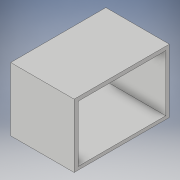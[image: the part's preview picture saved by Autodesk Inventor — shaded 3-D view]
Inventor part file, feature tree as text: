
AUTODESK INVENTOR PART (.ipt)
format: ipt  version: 2019 (Build 230136000, 136)  size: 93,696 bytes
history: native  units: mm
features: extrude x2, sketch x2
ambient origin geometry x8: Origin, YZ Plane, XZ Plane, XY Plane, X Axis, Y Axis, Z Axis, Center Point
bodies: Solid1 (feature_tree)
feature tree (4):
  extrude  "Extrusion1"  Depth=30.0mm
  extrude  "Extrusion2"  Depth=18.0mm TaperAngle=0.0deg
  sketch  "Sketch1"  dims[d0=20.0mm d1=30.0mm]
  sketch  "Sketch2"  dims[d2=20.0mm d3=0.0mm d4=18.0mm d5=0.0mm]
